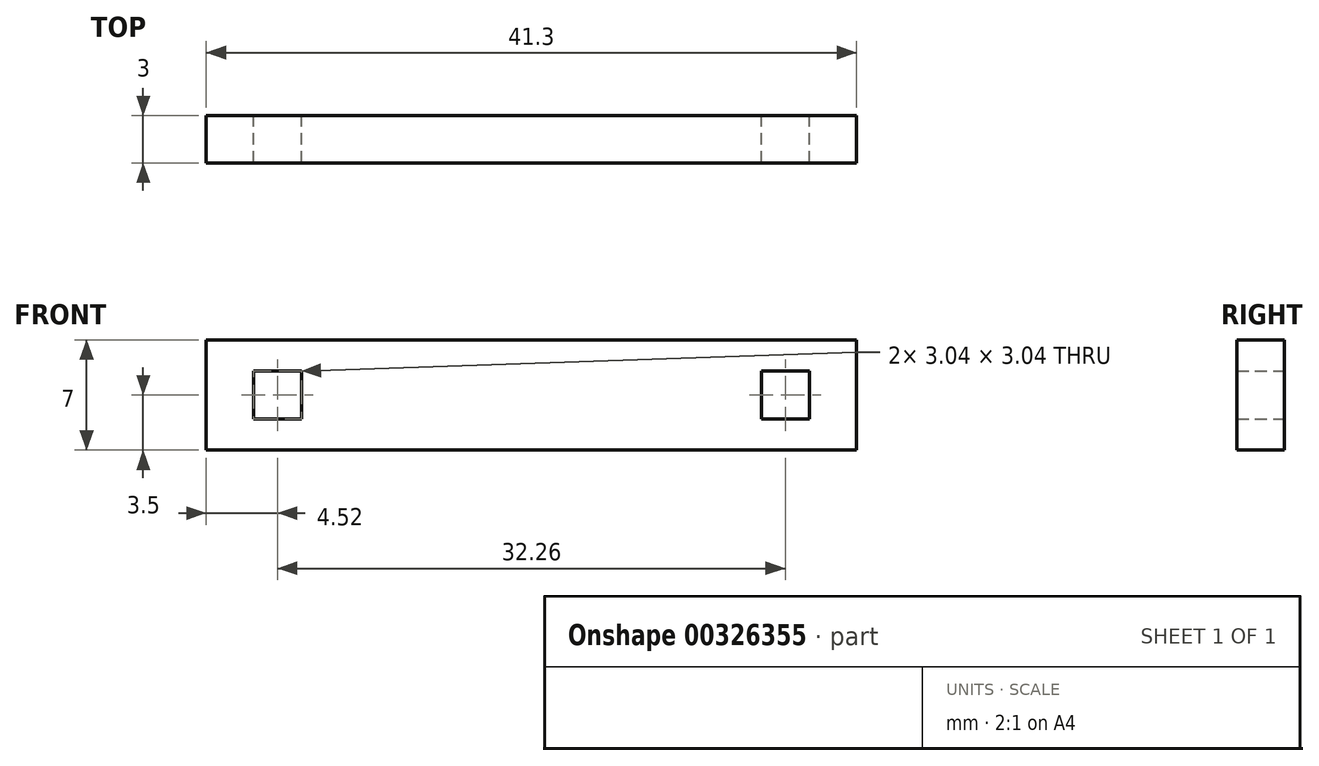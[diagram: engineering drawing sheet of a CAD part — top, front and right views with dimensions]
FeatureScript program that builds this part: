
annotation { "Feature Type Name" : "Feature", "Feature Type Description" : "" }
export const myFeature = defineFeature(function(context is Context, id is Id, definition is map)
    precondition{}
    {
        {
            var Q0;
            Q0=qCreatedBy(makeId("Front.planeOp"),FACE);
            var sketch = newSketch(context, id + "F0", { "sketchPlane" : qUnion([Q0])});
            skLineSegment(sketch, "E0", {"start": v(-22.17, 0) * mm, "end": v(19.13, 0) * mm});
            skLineSegment(sketch, "E1", {"start": v(19.13, 0) * mm, "end": v(19.13, 7) * mm});
            skLineSegment(sketch, "E2", {"start": v(19.13, 7) * mm, "end": v(-22.17, 7) * mm});
            skLineSegment(sketch, "E3", {"start": v(-22.17, 7) * mm, "end": v(-22.17, 0) * mm});
            skLineSegment(sketch, "E4.bottom", {"start": v(-19.17, 5.02) * mm, "end": v(-16.13, 5.02) * mm});
            skLineSegment(sketch, "E4.top", {"start": v(-19.17, 1.98) * mm, "end": v(-16.13, 1.98) * mm});
            skLineSegment(sketch, "E4.left", {"start": v(-19.17, 5.02) * mm, "end": v(-19.17, 1.98) * mm});
            skLineSegment(sketch, "E4.right", {"start": v(-16.13, 5.02) * mm, "end": v(-16.13, 1.98) * mm});
            skLineSegment(sketch, "E5.bottom", {"start": v(13.09, 5.02) * mm, "end": v(16.13, 5.02) * mm});
            skLineSegment(sketch, "E5.top", {"start": v(13.09, 1.98) * mm, "end": v(16.13, 1.98) * mm});
            skLineSegment(sketch, "E5.left", {"start": v(13.09, 5.02) * mm, "end": v(13.09, 1.98) * mm});
            skLineSegment(sketch, "E5.right", {"start": v(16.13, 5.02) * mm, "end": v(16.13, 1.98) * mm});
            skSolve(sketch);
        }
        {
            var Q0;
            Q0=makeQuery(id+"F0.imprint","IMPRINT",FACE,{"disambiguationData":[TD([[makeQuery(id+"F0.imprint","IMPRINT",EDGE,{"derivedFrom":sQuery(id+"F0.wireOp",EDGE,"E0")}),1.0]])]});
            extrude(context, id + "F1", {"entities" : qUnion([Q0]), "depth" : 3 * mm});
        }
    });
